# Revit family: Legrand_Transformateur_IP21_triphasé_400V-400V
name_source: partatom
category: Installations électriques
revit_build: Autodesk Revit 2018 (Build: 20170223_1515(x64)
units: mm (PartAtom-declared; Revit-internal decimal feet)

## family parameters
Basée sur le plan de construction = Non
Conserver l'orientation des annotations = Non
Cote de connecteur circulaire = Utiliser le diamètre
Couper avec des vides une fois chargée = Non
Numéro OmniClass = 23.80.00.00
Partagée = Non
Point de calcul de pièce = Non
Titre OmniClass = Electric Power and Lighting
Toujours verticalement = Oui
Type d'élément = Normal

## types (15) — shared parameters
Conditions Générale d'Utilisation = https://export.legrand.com
Fabricant = Legrand
Modèle = Transformateurs d'isolement triphasés
Tension primaire = 400 V en Δ
Tension secondaire = 400 V en Y +N
URL = www.legrand.com

## per-type parameters (varying)
| type | 042825 | 042826 | 042827 | 142828, 142829 | 142830, 142831 | 142832, 142833 | 142834, 142835 | 142836, 142837, 142838, 142839 | Poids | Section câble primaire | Section câble secondaire | Ucc (%) | diamètre de fixation | dimension A | dimension B | dimension C | fixation F | fixation G | perte totale max | perte à vide | puissance |
| Transformateur triphasé 142828 | Non | Non | Non | Oui | Non | Non | Non | Non | 126.00 kg | 35 mm² | 35 mm² | 3.7 | 11 mm  [stored 0.0360892 ft] | 590 mm  [stored 1.9357 ft] | 650 mm  [stored 2.13255 ft] | 500 mm  [stored 1.64042 ft] | 570 mm  [stored 1.87008 ft] | 146 mm  [stored 0.479003 ft] | 1069 W | 210 W | 25 kVA |
| Transformateur triphasé 142829 | Non | Non | Non | Oui | Non | Non | Non | Non | 174.00 kg | 35 mm² | 35 mm² | 3.6 | 11 mm  [stored 0.0360892 ft] | 590 mm  [stored 1.9357 ft] | 650 mm  [stored 2.13255 ft] | 500 mm  [stored 1.64042 ft] | 570 mm  [stored 1.87008 ft] | 176 mm  [stored 0.577428 ft] | 1550 W | 330 W | 40 kVA |
| Transformateur triphasé 142830 | Non | Non | Non | Non | Oui | Non | Non | Non | 247.00 kg | 35 mm² | 35 mm² | 5.5 | 16 mm  [stored 0.0524934 ft] | 670 mm  [stored 2.19816 ft] | 700 mm  [stored 2.29659 ft] | 610 mm  [stored 2.00131 ft] | 400 mm  [stored 1.31234 ft] | 580 mm  [stored 1.90289 ft] | 2768 W | 427 W | 50 kVA |
| Transformateur triphasé 142831 | Non | Non | Non | Non | Oui | Non | Non | Non | 271.00 kg | 35 mm² | 35 mm² | 5.4 | 16 mm  [stored 0.0524934 ft] | 670 mm  [stored 2.19816 ft] | 700 mm  [stored 2.29659 ft] | 610 mm  [stored 2.00131 ft] | 400 mm  [stored 1.31234 ft] | 580 mm  [stored 1.90289 ft] | 2798 W | 486 W | 63 kVA |
| Transformateur triphasé 142832 | Non | Non | Non | Non | Non | Oui | Non | Non | 336.00 kg | 70 mm² | 70 mm² | 4.9 | 16 mm  [stored 0.0524934 ft] | 670 mm  [stored 2.19816 ft] | 800 mm  [stored 2.62467 ft] | 740 mm  [stored 2.42782 ft] | 400 mm  [stored 1.31234 ft] | 687 mm  [stored 2.25394 ft] | 2777 W | 578 W | 80 kVA |
| Transformateur triphasé 142833 | Non | Non | Non | Non | Non | Oui | Non | Non | 407.00 kg | 120 mm² | 70 mm² | 3.9 | 16 mm  [stored 0.0524934 ft] | 670 mm  [stored 2.19816 ft] | 800 mm  [stored 2.62467 ft] | 740 mm  [stored 2.42782 ft] | 400 mm  [stored 1.31234 ft] | 687 mm  [stored 2.25394 ft] | 3260 W | 733 W | 100 kVA |
| Transformateur triphasé 142834 | Non | Non | Non | Non | Non | Non | Oui | Non | 457.00 kg | 120 mm² | 120 mm² | 3.3 | 16 mm  [stored 0.0524934 ft] | 820 mm  [stored 2.69029 ft] | 940 mm  [stored 3.08399 ft] | 880 mm  [stored 2.88714 ft] | 500 mm  [stored 1.64042 ft] | 820 mm  [stored 2.69029 ft] | 4083 W | 733 W | 125 kVA |
| Transformateur triphasé 142835 | Non | Non | Non | Non | Non | Non | Oui | Non | 475.00 kg | 150 mm² | 150 mm² | 3.7 | 16 mm  [stored 0.0524934 ft] | 820 mm  [stored 2.69029 ft] | 940 mm  [stored 3.08399 ft] | 880 mm  [stored 2.88714 ft] | 500 mm  [stored 1.64042 ft] | 820 mm  [stored 2.69029 ft] | 4823 W | 748 W | 160 kVA |
| Transformateur triphasé 142836 | Non | Non | Non | Non | Non | Non | Non | Oui | 656.00 kg | 200 mm² | 200 mm² | 4.3 | 20 mm  [stored 0.0656168 ft] | 1280 mm  [stored 4.19948 ft] | 1140 mm  [stored 3.74016 ft] | 990 mm  [stored 3.24803 ft] | 630 mm  [stored 2.06693 ft] | 940 mm  [stored 3.08399 ft] | 5794 W | 841 W | 200 kVA |
| Transformateur triphasé 142837 | Non | Non | Non | Non | Non | Non | Non | Oui | 699.00 kg | 200 mm² | 200 mm² | 5.8 | 20 mm  [stored 0.0656168 ft] | 1280 mm  [stored 4.19948 ft] | 1140 mm  [stored 3.74016 ft] | 990 mm  [stored 3.24803 ft] | 630 mm  [stored 2.06693 ft] | 940 mm  [stored 3.08399 ft] | 7501 W | 841 W | 250 kVA |
| Transformateur triphasé 142838 | Non | Non | Non | Non | Non | Non | Non | Oui | 818.00 kg | 250 mm² | 250 mm² | 4.6 | 20 mm  [stored 0.0656168 ft] | 1280 mm  [stored 4.19948 ft] | 1140 mm  [stored 3.74016 ft] | 990 mm  [stored 3.24803 ft] | 630 mm  [stored 2.06693 ft] | 940 mm  [stored 3.08399 ft] | 7308 W | 982 W | 315 kVA |
| Transformateur triphasé 142839 | Non | Non | Non | Non | Non | Non | Non | Oui | 1070.00 kg | 315mm² | 315 mm² | 3.9 | 20 mm  [stored 0.0656168 ft] | 1280 mm  [stored 4.19948 ft] | 1140 mm  [stored 3.74016 ft] | 990 mm  [stored 3.24803 ft] | 630 mm  [stored 2.06693 ft] | 940 mm  [stored 3.08399 ft] | 8838 W | 1372 W | 400 kVA |
| Transformateur triphasé 042825 | Oui | Non | Non | Non | Non | Non | Non | Non | 58.00 kg | 10 mm² | 10 mm² | 4.3 | 9 mm  [stored 0.0295276 ft] | 420 mm  [stored 1.37795 ft] | 390 mm  [stored 1.27953 ft] | 310 mm  [stored 1.01706 ft] | 400 mm  [stored 1.31234 ft] | 126 mm  [stored 0.413386 ft] | 389 W | 108 W | 6 kVA |
| Transformateur triphasé 042826 | Non | Oui | Non | Non | Non | Non | Non | Non | 81.20 kg | 10 mm² | 10 mm² | 3.7 | 9 mm  [stored 0.0295276 ft] | 470 mm  [stored 1.54199 ft] | 410 mm  [stored 1.34514 ft] | 310 mm  [stored 1.01706 ft] | 450 mm  [stored 1.47638 ft] | 146 mm  [stored 0.479003 ft] | 571 W | 188 W | 10 kVA |
| Transformateur triphasé 042827 | Non | Non | Oui | Non | Non | Non | Non | Non | 110.50 kg | 35 mm² | 35 mm² | 3.2 | 9 mm  [stored 0.0295276 ft] | 530 mm  [stored 1.73885 ft] | 460 mm  [stored 1.50919 ft] | 380 mm  [stored 1.24672 ft] | 510 mm  [stored 1.67323 ft] | 146 mm  [stored 0.479003 ft] | 76200 W | 256 W | 16 kVA |

note: [stored X ft] marks values corroborated as IEEE doubles in the binary element streams (Revit-internal decimal feet)
